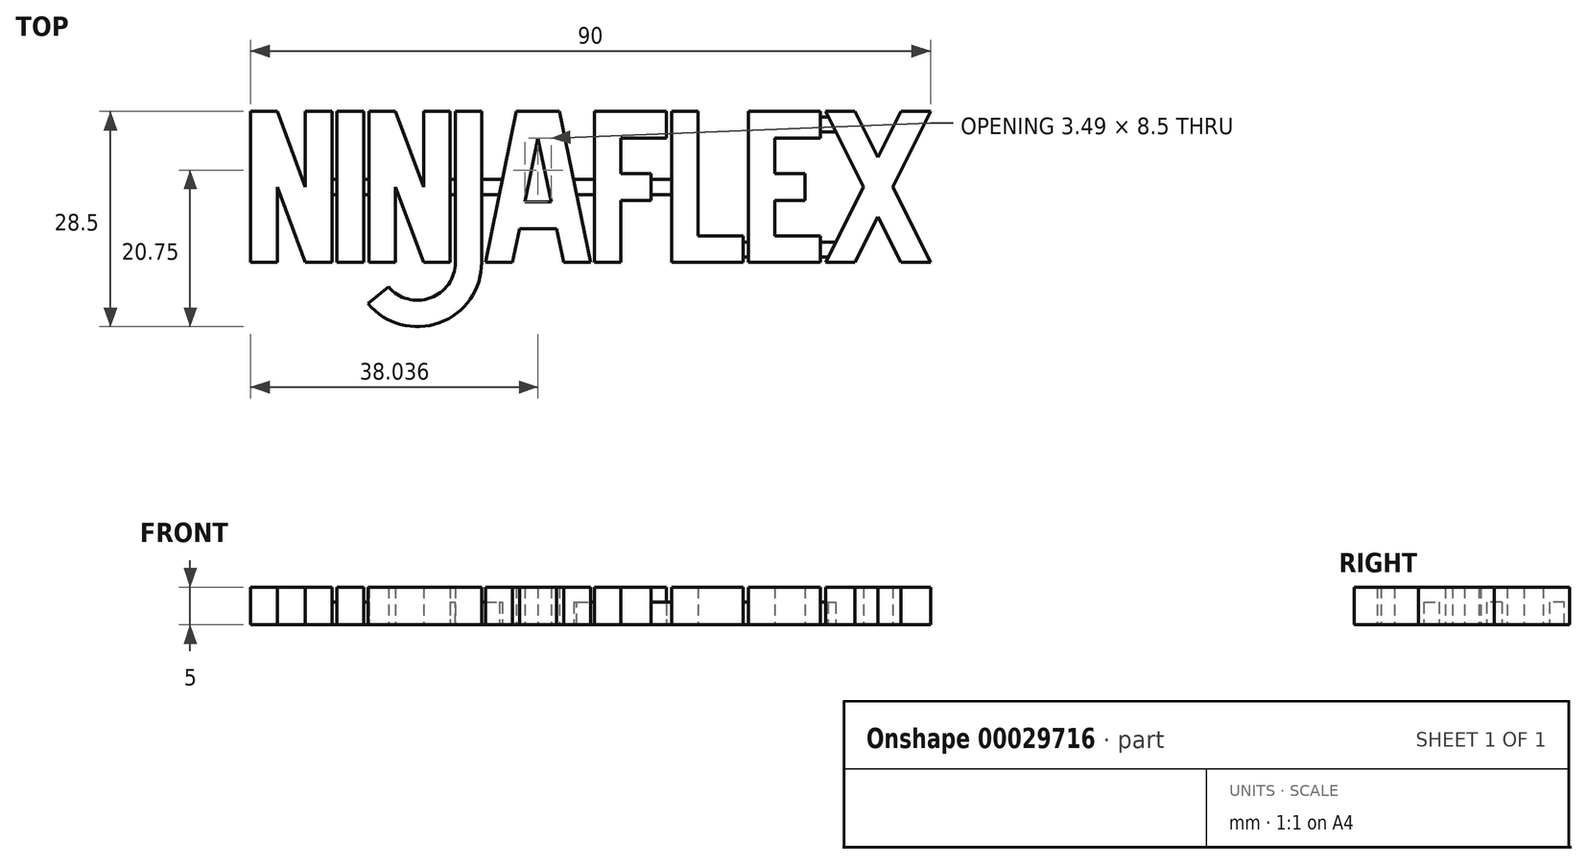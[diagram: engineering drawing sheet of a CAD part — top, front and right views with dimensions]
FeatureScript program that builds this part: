
annotation { "Feature Type Name" : "Feature", "Feature Type Description" : "" }
export const myFeature = defineFeature(function(context is Context, id is Id, definition is map)
    precondition{}
    {
        {
            var Q0;
            Q0=qCreatedBy(makeId("Top.planeOp"),FACE);
            var sketch = newSketch(context, id + "F0", { "sketchPlane" : qUnion([Q0])});
            skLineSegment(sketch, "E0.bottom", {"start": v(-45, 10) * mm, "end": v(45, 10) * mm, "construction": true});
            skLineSegment(sketch, "E0.top", {"start": v(-45, -10) * mm, "end": v(45, -10) * mm, "construction": true});
            skLineSegment(sketch, "E0.left", {"start": v(-45, 10) * mm, "end": v(-45, -10) * mm, "construction": true});
            skLineSegment(sketch, "E0.right", {"start": v(45, 10) * mm, "end": v(45, -10) * mm, "construction": true});
            skLineSegment(sketch, "E1", {"start": v(0, 10) * mm, "end": v(0, -10) * mm, "construction": true});
            skLineSegment(sketch, "E2", {"start": v(-45, -10) * mm, "end": v(-45, 10) * mm});
            skLineSegment(sketch, "E3", {"start": v(-45, 10) * mm, "end": v(-41.5, 10) * mm});
            skLineSegment(sketch, "E4", {"start": v(-41.5, 10) * mm, "end": v(-37.76, 0) * mm});
            skLineSegment(sketch, "E5", {"start": v(-37.76, 0) * mm, "end": v(-37.76, 10) * mm});
            skLineSegment(sketch, "E6", {"start": v(-37.76, 10) * mm, "end": v(-34.26, 10) * mm});
            skLineSegment(sketch, "E7", {"start": v(-34.26, 10) * mm, "end": v(-34.26, -10) * mm});
            skLineSegment(sketch, "E8", {"start": v(-34.26, -10) * mm, "end": v(-37.76, -10) * mm});
            skLineSegment(sketch, "E9", {"start": v(-37.76, -10) * mm, "end": v(-41.5, 0) * mm});
            skLineSegment(sketch, "E10", {"start": v(-41.5, 0) * mm, "end": v(-41.5, -10) * mm});
            skLineSegment(sketch, "E11", {"start": v(-41.5, -10) * mm, "end": v(-45, -10) * mm});
            skLineSegment(sketch, "E12", {"start": v(-40.35, -3.1) * mm, "end": v(-37.07, -1.87) * mm, "construction": true});
            skLineSegment(sketch, "E13.bottom", {"start": v(-33.56, 10) * mm, "end": v(-30.06, 10) * mm});
            skLineSegment(sketch, "E13.top", {"start": v(-33.56, -10) * mm, "end": v(-30.06, -10) * mm});
            skLineSegment(sketch, "E13.left", {"start": v(-33.56, 10) * mm, "end": v(-33.56, -10) * mm});
            skLineSegment(sketch, "E13.right", {"start": v(-30.06, 10) * mm, "end": v(-30.06, -10) * mm});
            skLineSegment(sketch, "E14", {"start": v(-29.36, -10) * mm, "end": v(-29.36, 10) * mm});
            skLineSegment(sketch, "E15", {"start": v(-29.36, 10) * mm, "end": v(-25.86, 10) * mm});
            skLineSegment(sketch, "E16", {"start": v(-25.86, 10) * mm, "end": v(-22.13, 0) * mm});
            skLineSegment(sketch, "E17", {"start": v(-22.13, 0) * mm, "end": v(-22.13, 10) * mm});
            skLineSegment(sketch, "E18", {"start": v(-22.13, 10) * mm, "end": v(-18.63, 10) * mm});
            skLineSegment(sketch, "E19", {"start": v(-18.63, 10) * mm, "end": v(-18.63, -10) * mm});
            skLineSegment(sketch, "E20", {"start": v(-18.63, -10) * mm, "end": v(-22.13, -10) * mm});
            skLineSegment(sketch, "E21", {"start": v(-22.13, -10) * mm, "end": v(-25.86, 0) * mm});
            skLineSegment(sketch, "E22", {"start": v(-25.86, 0) * mm, "end": v(-25.86, -10) * mm});
            skLineSegment(sketch, "E23", {"start": v(-25.86, -10) * mm, "end": v(-29.36, -10) * mm});
            skLineSegment(sketch, "E24", {"start": v(-25.86, 0) * mm, "end": v(-22.59, 1.23) * mm, "construction": true});
            skLineSegment(sketch, "E25", {"start": v(-34.26, 8.44) * mm, "end": v(-33.56, 8.44) * mm, "construction": true});
            skLineSegment(sketch, "E26", {"start": v(-30.06, 8.54) * mm, "end": v(-29.36, 8.54) * mm, "construction": true});
            skLineSegment(sketch, "E27", {"start": v(-41.5, 0) * mm, "end": v(-25.86, 0) * mm, "construction": true});
            skLineSegment(sketch, "E28.bottom", {"start": v(-17.93, 10) * mm, "end": v(-14.43, 10) * mm});
            skLineSegment(sketch, "E28.top", {"start": v(-17.93, -10) * mm, "end": v(-14.43, -10) * mm, "construction": true});
            skLineSegment(sketch, "E28.left", {"start": v(-17.93, 10) * mm, "end": v(-17.93, -10) * mm});
            skLineSegment(sketch, "E28.right", {"start": v(-14.43, 10) * mm, "end": v(-14.43, -10) * mm});
            skArc(sketch, "E29", {"start": v(-26.76, -13.21) * mm, "mid": v(-21.22, -14.7) * mm, "end": v(-17.93, -10) * mm});
            skArc(sketch, "E30", {"start": v(-29.44, -15.46) * mm, "mid": v(-20.02, -17.99) * mm, "end": v(-14.43, -10) * mm});
            skLineSegment(sketch, "E31", {"start": v(-29.44, -15.46) * mm, "end": v(-26.76, -13.21) * mm});
            skLineSegment(sketch, "E32", {"start": v(-18.63, 5.13) * mm, "end": v(-17.93, 5.13) * mm, "construction": true});
            skLineSegment(sketch, "E33", {"start": v(-13.93, -10) * mm, "end": v(-9.82, 10) * mm});
            skLineSegment(sketch, "E34", {"start": v(-9.82, 10) * mm, "end": v(-4.1, 10) * mm});
            skLineSegment(sketch, "E35", {"start": v(-4.1, 10) * mm, "end": v(0, -10) * mm});
            skLineSegment(sketch, "E36", {"start": v(0, -10) * mm, "end": v(-3.57, -10) * mm});
            skLineSegment(sketch, "E37", {"start": v(-3.57, -10) * mm, "end": v(-4.5, -5.5) * mm});
            skLineSegment(sketch, "E38", {"start": v(-4.5, -5.5) * mm, "end": v(-9.43, -5.5) * mm});
            skLineSegment(sketch, "E39", {"start": v(-9.43, -5.5) * mm, "end": v(-10.35, -10) * mm});
            skLineSegment(sketch, "E40", {"start": v(-10.35, -10) * mm, "end": v(-13.93, -10) * mm});
            skLineSegment(sketch, "E41", {"start": v(-6.96, -5.5) * mm, "end": v(-6.96, 10) * mm, "construction": true});
            skLineSegment(sketch, "E42", {"start": v(-6.96, 6.5) * mm, "end": v(-8.71, -2) * mm});
            skLineSegment(sketch, "E43", {"start": v(-8.71, -2) * mm, "end": v(-5.22, -2) * mm});
            skLineSegment(sketch, "E44", {"start": v(-5.22, -2) * mm, "end": v(-6.96, 6.5) * mm});
            skLineSegment(sketch, "E45", {"start": v(-10.35, -10) * mm, "end": v(-13.78, -9.3) * mm, "construction": true});
            skLineSegment(sketch, "E46", {"start": v(-5.22, -2) * mm, "end": v(-5.22, -5.5) * mm, "construction": true});
            skLineSegment(sketch, "E47", {"start": v(-13.93, 6.5) * mm, "end": v(-13.93, 10) * mm, "construction": true});
            skLineSegment(sketch, "E48", {"start": v(31.1, 10) * mm, "end": v(31.1, -10) * mm, "construction": true});
            skLineSegment(sketch, "E49", {"start": v(38.05, 10) * mm, "end": v(38.05, 0) * mm, "construction": true});
            skLineSegment(sketch, "E50", {"start": v(38.05, 0) * mm, "end": v(45, 0) * mm, "construction": true});
            skLineSegment(sketch, "E51", {"start": v(45, 10) * mm, "end": v(41.09, 10) * mm});
            skLineSegment(sketch, "E52", {"start": v(41.09, 10) * mm, "end": v(38.05, 3.92) * mm});
            skLineSegment(sketch, "E53", {"start": v(45, 10) * mm, "end": v(40, 0) * mm});
            skLineSegment(sketch, "E54", {"start": v(38.05, 3.92) * mm, "end": v(41.18, 2.35) * mm, "construction": true});
            skLineSegment(sketch, "E55.MirrorCS", {"start": v(35.01, 10) * mm, "end": v(38.05, 3.92) * mm});
            skLineSegment(sketch, "E56.MirrorCS", {"start": v(31.1, 10) * mm, "end": v(35.01, 10) * mm});
            skLineSegment(sketch, "E57.MirrorCS", {"start": v(31.1, 10) * mm, "end": v(36.1, 0) * mm});
            skLineSegment(sketch, "E58.MirrorCS", {"start": v(45, -10) * mm, "end": v(40, 0) * mm});
            skLineSegment(sketch, "E59.MirrorCS", {"start": v(45, -10) * mm, "end": v(41.09, -10) * mm});
            skLineSegment(sketch, "E60.MirrorCS", {"start": v(41.09, -10) * mm, "end": v(38.05, -3.92) * mm});
            skLineSegment(sketch, "E61.MirrorCS", {"start": v(35.01, -10) * mm, "end": v(38.05, -3.92) * mm});
            skLineSegment(sketch, "E62.MirrorCS", {"start": v(31.1, -10) * mm, "end": v(35.01, -10) * mm});
            skLineSegment(sketch, "E63.MirrorCS", {"start": v(31.1, -10) * mm, "end": v(36.1, 0) * mm});
            skLineSegment(sketch, "E64", {"start": v(20.9, 10) * mm, "end": v(30.4, 10) * mm});
            skLineSegment(sketch, "E65", {"start": v(30.4, 10) * mm, "end": v(30.4, 6.5) * mm});
            skLineSegment(sketch, "E66", {"start": v(30.4, 6.5) * mm, "end": v(24.4, 6.5) * mm});
            skLineSegment(sketch, "E67", {"start": v(24.4, 6.5) * mm, "end": v(24.4, 1.75) * mm});
            skLineSegment(sketch, "E68", {"start": v(24.4, 1.75) * mm, "end": v(28.4, 1.75) * mm});
            skLineSegment(sketch, "E69.MirrorCS", {"start": v(24.4, -1.75) * mm, "end": v(28.4, -1.75) * mm});
            skLineSegment(sketch, "E70.MirrorCS", {"start": v(24.4, -6.5) * mm, "end": v(24.4, -1.75) * mm});
            skLineSegment(sketch, "E71.MirrorCS", {"start": v(30.4, -6.5) * mm, "end": v(24.4, -6.5) * mm});
            skLineSegment(sketch, "E72.MirrorCS", {"start": v(30.4, -10) * mm, "end": v(30.4, -6.5) * mm});
            skLineSegment(sketch, "E73.MirrorCS", {"start": v(20.9, -10) * mm, "end": v(30.4, -10) * mm});
            skLineSegment(sketch, "E74", {"start": v(28.4, 1.75) * mm, "end": v(28.4, -1.75) * mm});
            skLineSegment(sketch, "E75", {"start": v(20.9, -10) * mm, "end": v(20.9, 10) * mm});
            skLineSegment(sketch, "E76", {"start": v(24.4, 6.5) * mm, "end": v(20.9, 6.5) * mm, "construction": true});
            skLineSegment(sketch, "E77", {"start": v(30.4, 6.5) * mm, "end": v(31.1, 6.5) * mm, "construction": true});
            skLineSegment(sketch, "E78", {"start": v(0.5, -10) * mm, "end": v(0.5, 10) * mm});
            skLineSegment(sketch, "E79", {"start": v(0.5, 10) * mm, "end": v(10, 10) * mm});
            skLineSegment(sketch, "E80", {"start": v(10, 10) * mm, "end": v(10, 6.5) * mm});
            skLineSegment(sketch, "E81", {"start": v(10, 6.5) * mm, "end": v(4, 6.5) * mm});
            skLineSegment(sketch, "E82", {"start": v(4, 6.5) * mm, "end": v(4, 1.75) * mm});
            skLineSegment(sketch, "E83", {"start": v(4, 1.75) * mm, "end": v(8, 1.75) * mm});
            skLineSegment(sketch, "E84", {"start": v(8, 1.75) * mm, "end": v(8, -1.75) * mm});
            skLineSegment(sketch, "E85", {"start": v(8, -1.75) * mm, "end": v(4, -1.75) * mm});
            skLineSegment(sketch, "E86", {"start": v(4, -1.75) * mm, "end": v(4, -10) * mm});
            skLineSegment(sketch, "E87", {"start": v(4, -10) * mm, "end": v(0.5, -10) * mm});
            skLineSegment(sketch, "E88", {"start": v(4, 6.5) * mm, "end": v(0.5, 6.5) * mm, "construction": true});
            skLineSegment(sketch, "E89", {"start": v(-13.93, 6.5) * mm, "end": v(-14.43, 6.5) * mm, "construction": true});
            skLineSegment(sketch, "E90", {"start": v(0, -10) * mm, "end": v(0, -6.37) * mm, "construction": true});
            skLineSegment(sketch, "E91", {"start": v(0, -6.37) * mm, "end": v(0.5, -6.37) * mm, "construction": true});
            skLineSegment(sketch, "E92", {"start": v(10.7, 10) * mm, "end": v(10.7, -10) * mm});
            skLineSegment(sketch, "E93", {"start": v(10.7, -10) * mm, "end": v(20.2, -10) * mm});
            skLineSegment(sketch, "E94", {"start": v(20.2, -10) * mm, "end": v(20.2, -6.5) * mm});
            skLineSegment(sketch, "E95", {"start": v(20.2, -6.5) * mm, "end": v(14.2, -6.5) * mm});
            skLineSegment(sketch, "E96", {"start": v(14.2, -6.5) * mm, "end": v(14.2, 10) * mm});
            skLineSegment(sketch, "E97", {"start": v(14.2, 10) * mm, "end": v(10.7, 10) * mm});
            skLineSegment(sketch, "E98", {"start": v(10, 6.5) * mm, "end": v(10.7, 6.5) * mm, "construction": true});
            skLineSegment(sketch, "E99", {"start": v(20.2, -6.5) * mm, "end": v(20.9, -6.5) * mm, "construction": true});
            skSolve(sketch);
        }
        {
            var Q0;
            Q0=makeQuery(id+"F0.imprint","IMPRINT",FACE,{"disambiguationData":[TD([[makeQuery(id+"F0.imprint","IMPRINT",EDGE,{"derivedFrom":sQuery(id+"F0.wireOp",EDGE,"E2")}),-1.0]])]});
            var Q1;
            Q1=makeQuery(id+"F0.imprint","IMPRINT",FACE,{"disambiguationData":[TD([[makeQuery(id+"F0.imprint","IMPRINT",EDGE,{"derivedFrom":sQuery(id+"F0.wireOp",EDGE,"E13.bottom")}),-1.0]])]});
            var Q2;
            Q2=makeQuery(id+"F0.imprint","IMPRINT",FACE,{"disambiguationData":[TD([[makeQuery(id+"F0.imprint","IMPRINT",EDGE,{"derivedFrom":sQuery(id+"F0.wireOp",EDGE,"E14")}),-1.0]])]});
            var Q3;
            Q3=makeQuery(id+"F0.imprint","IMPRINT",FACE,{"disambiguationData":[TD([[makeQuery(id+"F0.imprint","IMPRINT",EDGE,{"derivedFrom":sQuery(id+"F0.wireOp",EDGE,"E28.bottom")}),-1.0]])]});
            var Q4;
            Q4=makeQuery(id+"F0.imprint","IMPRINT",FACE,{"disambiguationData":[TD([[makeQuery(id+"F0.imprint","IMPRINT",EDGE,{"derivedFrom":sQuery(id+"F0.wireOp",EDGE,"E51")}),1.0]])]});
            var Q5;
            Q5=makeQuery(id+"F0.imprint","IMPRINT",FACE,{"disambiguationData":[TD([[makeQuery(id+"F0.imprint","IMPRINT",EDGE,{"derivedFrom":sQuery(id+"F0.wireOp",EDGE,"E64")}),-1.0]])]});
            var Q6;
            Q6=makeQuery(id+"F0.imprint","IMPRINT",FACE,{"disambiguationData":[TD([[makeQuery(id+"F0.imprint","IMPRINT",EDGE,{"derivedFrom":sQuery(id+"F0.wireOp",EDGE,"E78")}),-1.0]])]});
            var Q7;
            Q7=makeQuery(id+"F0.imprint","IMPRINT",FACE,{"disambiguationData":[TD([[makeQuery(id+"F0.imprint","IMPRINT",EDGE,{"derivedFrom":sQuery(id+"F0.wireOp",EDGE,"E92")}),1.0]])]});
            var Q8;
            Q8=makeQuery(id+"F0.imprint","IMPRINT",FACE,{"disambiguationData":[TD([[makeQuery(id+"F0.imprint","IMPRINT",EDGE,{"derivedFrom":sQuery(id+"F0.wireOp",EDGE,"E33")}),-1.0]])]});
            extrude(context, id + "F1", {"entities" : qUnion([Q0, Q1, Q2, Q3, Q4, Q5, Q6, Q7, Q8]), "depth" : 5 * mm});
        }
        {
            var Q0;
            Q0=qCreatedBy(makeId("Top.planeOp"),FACE);
            var sketch = newSketch(context, id + "F2", { "sketchPlane" : qUnion([Q0])});
            skLineSegment(sketch, "E100.bottom", {"start": v(-34.26, 1) * mm, "end": v(-29.36, 1) * mm});
            skLineSegment(sketch, "E100.top", {"start": v(-34.26, -1) * mm, "end": v(-29.36, -1) * mm});
            skLineSegment(sketch, "E100.left", {"start": v(-34.26, 1) * mm, "end": v(-34.26, -1) * mm});
            skLineSegment(sketch, "E100.right", {"start": v(-29.36, 1) * mm, "end": v(-29.36, -1) * mm});
            skLineSegment(sketch, "E101.bottom", {"start": v(-18.63, 1) * mm, "end": v(-11.67, 1) * mm});
            skLineSegment(sketch, "E101.top", {"start": v(-18.63, -1) * mm, "end": v(-11.67, -1) * mm});
            skLineSegment(sketch, "E101.left", {"start": v(-18.63, 1) * mm, "end": v(-18.63, -1) * mm});
            skLineSegment(sketch, "E101.right", {"start": v(-11.67, 1) * mm, "end": v(-11.67, -1) * mm});
            skLineSegment(sketch, "E102.bottom", {"start": v(-2.26, 1) * mm, "end": v(0.5, 1) * mm});
            skLineSegment(sketch, "E102.top", {"start": v(-2.26, -1) * mm, "end": v(0.5, -1) * mm});
            skLineSegment(sketch, "E102.left", {"start": v(-2.26, 1) * mm, "end": v(-2.26, -1) * mm});
            skLineSegment(sketch, "E102.right", {"start": v(0.5, 1) * mm, "end": v(0.5, -1) * mm});
            skLineSegment(sketch, "E103.bottom", {"start": v(20.2, -7.3) * mm, "end": v(20.9, -7.3) * mm});
            skLineSegment(sketch, "E103.top", {"start": v(20.2, -9.3) * mm, "end": v(20.9, -9.3) * mm});
            skLineSegment(sketch, "E103.left", {"start": v(20.2, -7.3) * mm, "end": v(20.2, -9.3) * mm});
            skLineSegment(sketch, "E103.right", {"start": v(20.9, -7.3) * mm, "end": v(20.9, -9.3) * mm});
            skLineSegment(sketch, "E104.bottom", {"start": v(30.4, 9.3) * mm, "end": v(32.45, 9.3) * mm});
            skLineSegment(sketch, "E104.top", {"start": v(30.4, 7.3) * mm, "end": v(32.45, 7.3) * mm});
            skLineSegment(sketch, "E104.left", {"start": v(30.4, 9.3) * mm, "end": v(30.4, 7.3) * mm});
            skLineSegment(sketch, "E104.right", {"start": v(32.45, 9.3) * mm, "end": v(32.45, 7.3) * mm});
            skLineSegment(sketch, "E105.bottom", {"start": v(30.4, -7.3) * mm, "end": v(32.45, -7.3) * mm});
            skLineSegment(sketch, "E105.top", {"start": v(30.4, -9.3) * mm, "end": v(32.45, -9.3) * mm});
            skLineSegment(sketch, "E105.left", {"start": v(30.4, -7.3) * mm, "end": v(30.4, -9.3) * mm});
            skLineSegment(sketch, "E105.right", {"start": v(32.45, -7.3) * mm, "end": v(32.45, -9.3) * mm});
            skLineSegment(sketch, "E106", {"start": v(0, 0) * mm, "end": v(-6.36, 0) * mm, "construction": true});
            skLineSegment(sketch, "E107.bottom", {"start": v(8, 1) * mm, "end": v(10.7, 1) * mm});
            skLineSegment(sketch, "E107.top", {"start": v(8, -1) * mm, "end": v(10.7, -1) * mm});
            skLineSegment(sketch, "E107.left", {"start": v(8, 1) * mm, "end": v(8, -1) * mm});
            skLineSegment(sketch, "E107.right", {"start": v(10.7, 1) * mm, "end": v(10.7, -1) * mm});
            skSolve(sketch);
        }
        {
            var Q0;
            Q0 = qSketchRegion(id + "F2", true);
            extrude(context, id + "F3", {"entities" : qUnion([Q0]), "operationType" : NewBodyOperationType.ADD, "depth" : 3 * mm});
        }
    });
